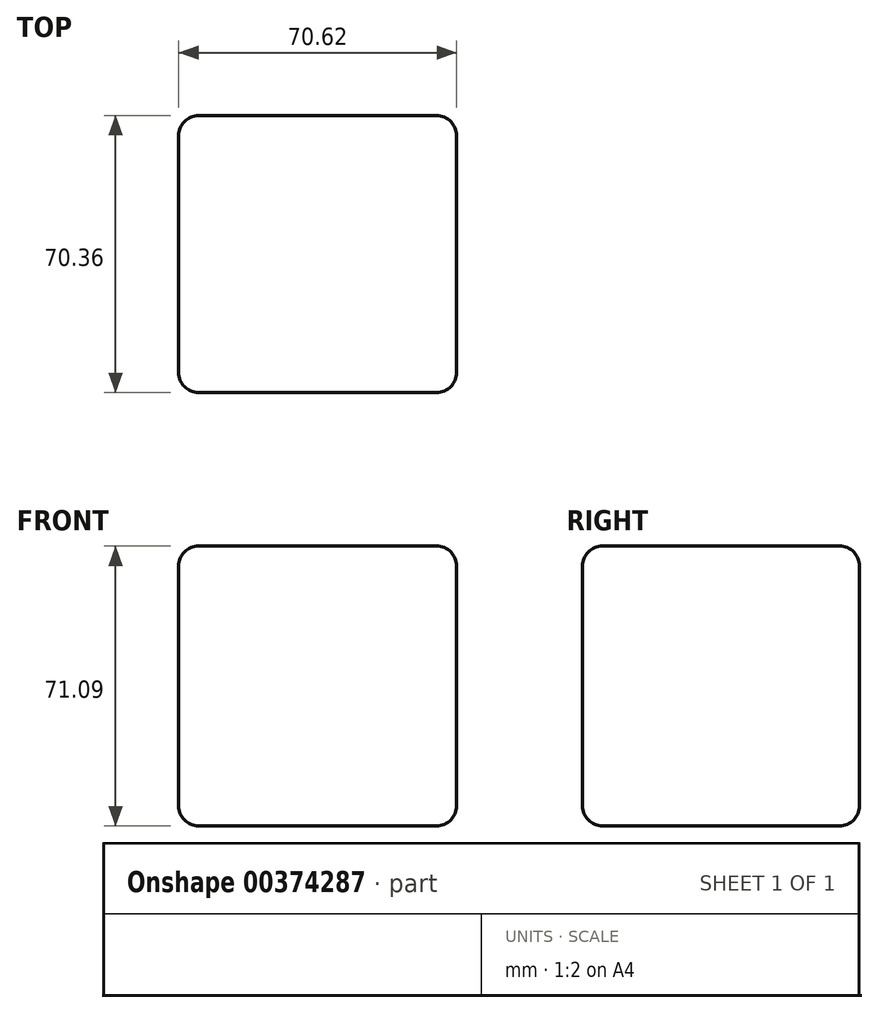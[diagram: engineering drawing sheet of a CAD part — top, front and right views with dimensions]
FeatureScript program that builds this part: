
annotation { "Feature Type Name" : "Feature", "Feature Type Description" : "" }
export const myFeature = defineFeature(function(context is Context, id is Id, definition is map)
    precondition{}
    {
        {
            var Q0;
            Q0=qCreatedBy(makeId("Front.planeOp"),FACE);
            var sketch = newSketch(context, id + "F0", { "sketchPlane" : qUnion([Q0])});
            skLineSegment(sketch, "E0.bottom", {"start": v(-33.02, 33.74) * mm, "end": v(37.6, 33.74) * mm});
            skLineSegment(sketch, "E0.top", {"start": v(-33.02, -37.35) * mm, "end": v(37.6, -37.35) * mm});
            skLineSegment(sketch, "E0.left", {"start": v(-33.02, 33.74) * mm, "end": v(-33.02, -37.35) * mm});
            skLineSegment(sketch, "E0.right", {"start": v(37.6, 33.74) * mm, "end": v(37.6, -37.35) * mm});
            skSolve(sketch);
        }
        {
            var Q0;
            Q0=makeQuery(id+"F0.imprint","IMPRINT",FACE,{"disambiguationData":[TD([[makeQuery(id+"F0.imprint","IMPRINT",EDGE,{"derivedFrom":sQuery(id+"F0.wireOp",EDGE,"E0.bottom")}),-1.0]])]});
            extrude(context, id + "F1", {"entities" : qUnion([Q0]), "depth" : 70.36 * mm});
        }
        {
            var Q0;
            Q0=makeQuery(id+"F1.opExtrude","SWEPT_EDGE",EDGE,{"disambiguationData":[OSD([sQuery(id+"F0.wireOp",EDGE,"E0.bottom"),sQuery(id+"F0.wireOp",EDGE,"E0.right")])]});
            var Q1;
            Q1=makeQuery(id+"F1.opExtrude","CAP_EDGE",EDGE,{"disambiguationData":[OSD([sQuery(id+"F0.wireOp",EDGE,"E0.bottom")])],"isStart":false});
            var Q2;
            Q2=makeQuery(id+"F1.opExtrude","SWEPT_EDGE",EDGE,{"disambiguationData":[OSD([sQuery(id+"F0.wireOp",EDGE,"E0.bottom"),sQuery(id+"F0.wireOp",EDGE,"E0.left")])]});
            var Q3;
            Q3=makeQuery(id+"F1.opExtrude","CAP_EDGE",EDGE,{"disambiguationData":[OSD([sQuery(id+"F0.wireOp",EDGE,"E0.bottom")])],"isStart":true});
            var Q4;
            Q4=makeQuery(id+"F1.opExtrude","CAP_EDGE",EDGE,{"disambiguationData":[OSD([sQuery(id+"F0.wireOp",EDGE,"E0.right")])],"isStart":false});
            var Q5;
            Q5=makeQuery(id+"F1.opExtrude","CAP_EDGE",EDGE,{"disambiguationData":[OSD([sQuery(id+"F0.wireOp",EDGE,"E0.right")])],"isStart":true});
            var Q6;
            Q6=makeQuery(id+"F1.opExtrude","CAP_EDGE",EDGE,{"disambiguationData":[OSD([sQuery(id+"F0.wireOp",EDGE,"E0.left")])],"isStart":true});
            var Q7;
            Q7=makeQuery(id+"F1.opExtrude","CAP_EDGE",EDGE,{"disambiguationData":[OSD([sQuery(id+"F0.wireOp",EDGE,"E0.left")])],"isStart":false});
            var Q8;
            Q8=makeQuery(id+"F1.opExtrude","CAP_EDGE",EDGE,{"disambiguationData":[OSD([sQuery(id+"F0.wireOp",EDGE,"E0.top")])],"isStart":false});
            var Q9;
            Q9=makeQuery(id+"F1.opExtrude","SWEPT_EDGE",EDGE,{"disambiguationData":[OSD([sQuery(id+"F0.wireOp",EDGE,"E0.top"),sQuery(id+"F0.wireOp",EDGE,"E0.right")])]});
            var Q10;
            Q10=makeQuery(id+"F1.opExtrude","CAP_EDGE",EDGE,{"disambiguationData":[OSD([sQuery(id+"F0.wireOp",EDGE,"E0.top")])],"isStart":true});
            var Q11;
            Q11=makeQuery(id+"F1.opExtrude","SWEPT_EDGE",EDGE,{"disambiguationData":[OSD([sQuery(id+"F0.wireOp",EDGE,"E0.top"),sQuery(id+"F0.wireOp",EDGE,"E0.left")])]});
            fillet(context, id + "F2", {"entities" : qUnion([Q0, Q1, Q2, Q3, Q4, Q5, Q6, Q7, Q8, Q9, Q10, Q11]), "radius" : 5.08 * mm, "tangentPropagation" : true, "allowEdgeOverflow" : false});
        }
    });
